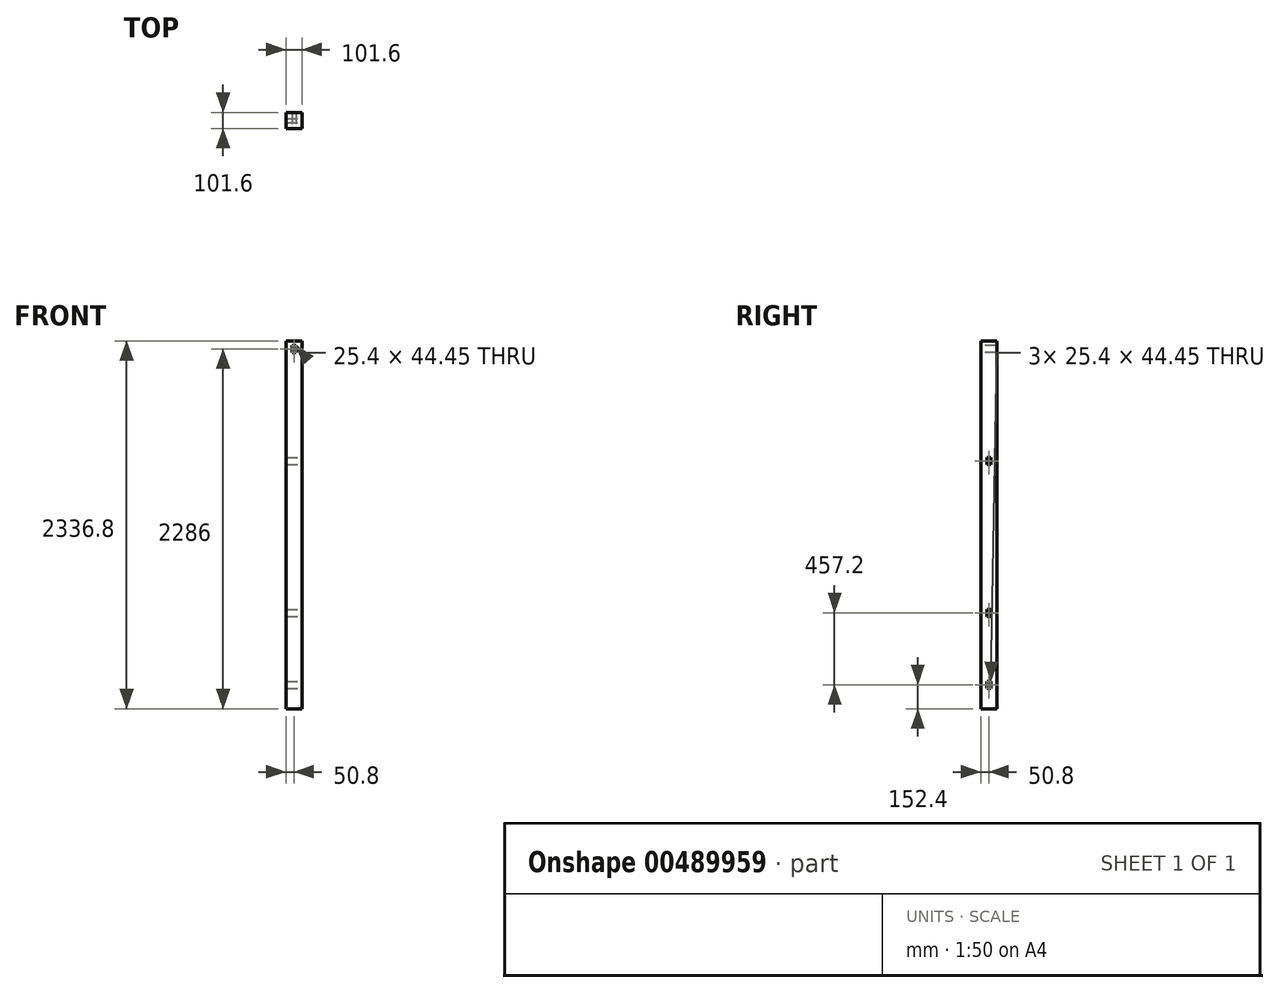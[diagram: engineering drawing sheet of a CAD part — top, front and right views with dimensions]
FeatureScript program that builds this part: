
annotation { "Feature Type Name" : "Feature", "Feature Type Description" : "" }
export const myFeature = defineFeature(function(context is Context, id is Id, definition is map)
    precondition{}
    {
        {
            var Q0;
            Q0=qCreatedBy(makeId("Top.planeOp"),FACE);
            var sketch = newSketch(context, id + "F0", { "sketchPlane" : qUnion([Q0])});
            skLineSegment(sketch, "E0.bottom", {"start": v(50.8, -50.8) * mm, "end": v(-50.8, -50.8) * mm});
            skLineSegment(sketch, "E0.top", {"start": v(50.8, 50.8) * mm, "end": v(-50.8, 50.8) * mm});
            skLineSegment(sketch, "E0.left", {"start": v(50.8, -50.8) * mm, "end": v(50.8, 50.8) * mm});
            skLineSegment(sketch, "E0.right", {"start": v(-50.8, -50.8) * mm, "end": v(-50.8, 50.8) * mm});
            skPoint(sketch, "E0.middle", {"position": v(0, 0) * mm});
            skSolve(sketch);
        }
        {
            var Q0;
            Q0 = qSketchRegion(id + "F0", true);
            extrude(context, id + "F1", {"entities" : qUnion([Q0]), "endBound" : BoundingType.SYMMETRIC, "depth" : 2336.8 * mm});
        }
        {
            var Q0;
            Q0=makeQuery(id+"F1.opExtrude","SWEPT_FACE",FACE,{"disambiguationData":[OSD([sQuery(id+"F0.wireOp",EDGE,"E0.bottom")])]});
            var sketch = newSketch(context, id + "F2", { "sketchPlane" : qUnion([Q0])});
            skLineSegment(sketch, "E1.bottom", {"start": v(12.7, 1095.38) * mm, "end": v(-12.7, 1095.38) * mm});
            skLineSegment(sketch, "E1.top", {"start": v(12.7, 1139.83) * mm, "end": v(-12.7, 1139.83) * mm});
            skLineSegment(sketch, "E1.left", {"start": v(12.7, 1095.38) * mm, "end": v(12.7, 1139.83) * mm});
            skLineSegment(sketch, "E1.right", {"start": v(-12.7, 1095.38) * mm, "end": v(-12.7, 1139.83) * mm});
            skPoint(sketch, "E1.middle", {"position": v(0, 1117.6) * mm});
            skSolve(sketch);
        }
        {
            var Q0;
            Q0 = qSketchRegion(id + "F2", true);
            extrude(context, id + "F3", {"entities" : qUnion([Q0]), "operationType" : NewBodyOperationType.REMOVE, "endBound" : BoundingType.THROUGH_ALL, "oppositeDirection" : true, "depth" : 25.4 * mm});
        }
        {
            var Q0;
            Q0=makeQuery(id+"F1.opExtrude","SWEPT_FACE",FACE,{"disambiguationData":[OSD([sQuery(id+"F0.wireOp",EDGE,"E0.left")])]});
            var sketch = newSketch(context, id + "F4", { "sketchPlane" : qUnion([Q0])});
            skLineSegment(sketch, "E2.bottom", {"start": v(12.7, 428.63) * mm, "end": v(-12.7, 428.63) * mm});
            skLineSegment(sketch, "E2.top", {"start": v(12.7, 384.18) * mm, "end": v(-12.7, 384.18) * mm});
            skLineSegment(sketch, "E2.left", {"start": v(12.7, 428.63) * mm, "end": v(12.7, 384.18) * mm});
            skLineSegment(sketch, "E2.right", {"start": v(-12.7, 428.63) * mm, "end": v(-12.7, 384.18) * mm});
            skPoint(sketch, "E2.middle", {"position": v(0, 406.4) * mm});
            skSolve(sketch);
        }
        {
            var Q0;
            Q0 = qSketchRegion(id + "F4", true);
            extrude(context, id + "F5", {"entities" : qUnion([Q0]), "operationType" : NewBodyOperationType.REMOVE, "endBound" : BoundingType.THROUGH_ALL, "oppositeDirection" : true, "depth" : 25.4 * mm});
        }
        {
            var Q0;
            Q0=makeQuery(id+"F1.opExtrude","SWEPT_FACE",FACE,{"disambiguationData":[OSD([sQuery(id+"F0.wireOp",EDGE,"E0.left")])]});
            var sketch = newSketch(context, id + "F6", { "sketchPlane" : qUnion([Q0])});
            skLineSegment(sketch, "E3.bottom", {"start": v(12.7, -536.58) * mm, "end": v(-12.7, -536.58) * mm});
            skLineSegment(sketch, "E3.top", {"start": v(12.7, -581.02) * mm, "end": v(-12.7, -581.02) * mm});
            skLineSegment(sketch, "E3.left", {"start": v(12.7, -536.58) * mm, "end": v(12.7, -581.02) * mm});
            skLineSegment(sketch, "E3.right", {"start": v(-12.7, -536.58) * mm, "end": v(-12.7, -581.02) * mm});
            skPoint(sketch, "E3.middle", {"position": v(0, -558.8) * mm});
            skSolve(sketch);
        }
        {
            var Q0;
            Q0 = qSketchRegion(id + "F6", true);
            extrude(context, id + "F7", {"entities" : qUnion([Q0]), "operationType" : NewBodyOperationType.REMOVE, "endBound" : BoundingType.THROUGH_ALL, "oppositeDirection" : true, "depth" : 25.4 * mm});
        }
        {
            var Q0;
            Q0=makeQuery(id+"F1.opExtrude","SWEPT_FACE",FACE,{"disambiguationData":[OSD([sQuery(id+"F0.wireOp",EDGE,"E0.left")])]});
            var sketch = newSketch(context, id + "F8", { "sketchPlane" : qUnion([Q0])});
            skLineSegment(sketch, "E4.bottom", {"start": v(-12.7, -993.77) * mm, "end": v(12.7, -993.77) * mm});
            skLineSegment(sketch, "E4.top", {"start": v(-12.7, -1038.22) * mm, "end": v(12.7, -1038.22) * mm});
            skLineSegment(sketch, "E4.left", {"start": v(-12.7, -993.77) * mm, "end": v(-12.7, -1038.22) * mm});
            skLineSegment(sketch, "E4.right", {"start": v(12.7, -993.77) * mm, "end": v(12.7, -1038.22) * mm});
            skPoint(sketch, "E4.middle", {"position": v(0, -1016) * mm});
            skSolve(sketch);
        }
        {
            var Q0;
            Q0 = qSketchRegion(id + "F8", true);
            extrude(context, id + "F9", {"entities" : qUnion([Q0]), "operationType" : NewBodyOperationType.REMOVE, "endBound" : BoundingType.THROUGH_ALL, "oppositeDirection" : true, "depth" : 25.4 * mm});
        }
    });
